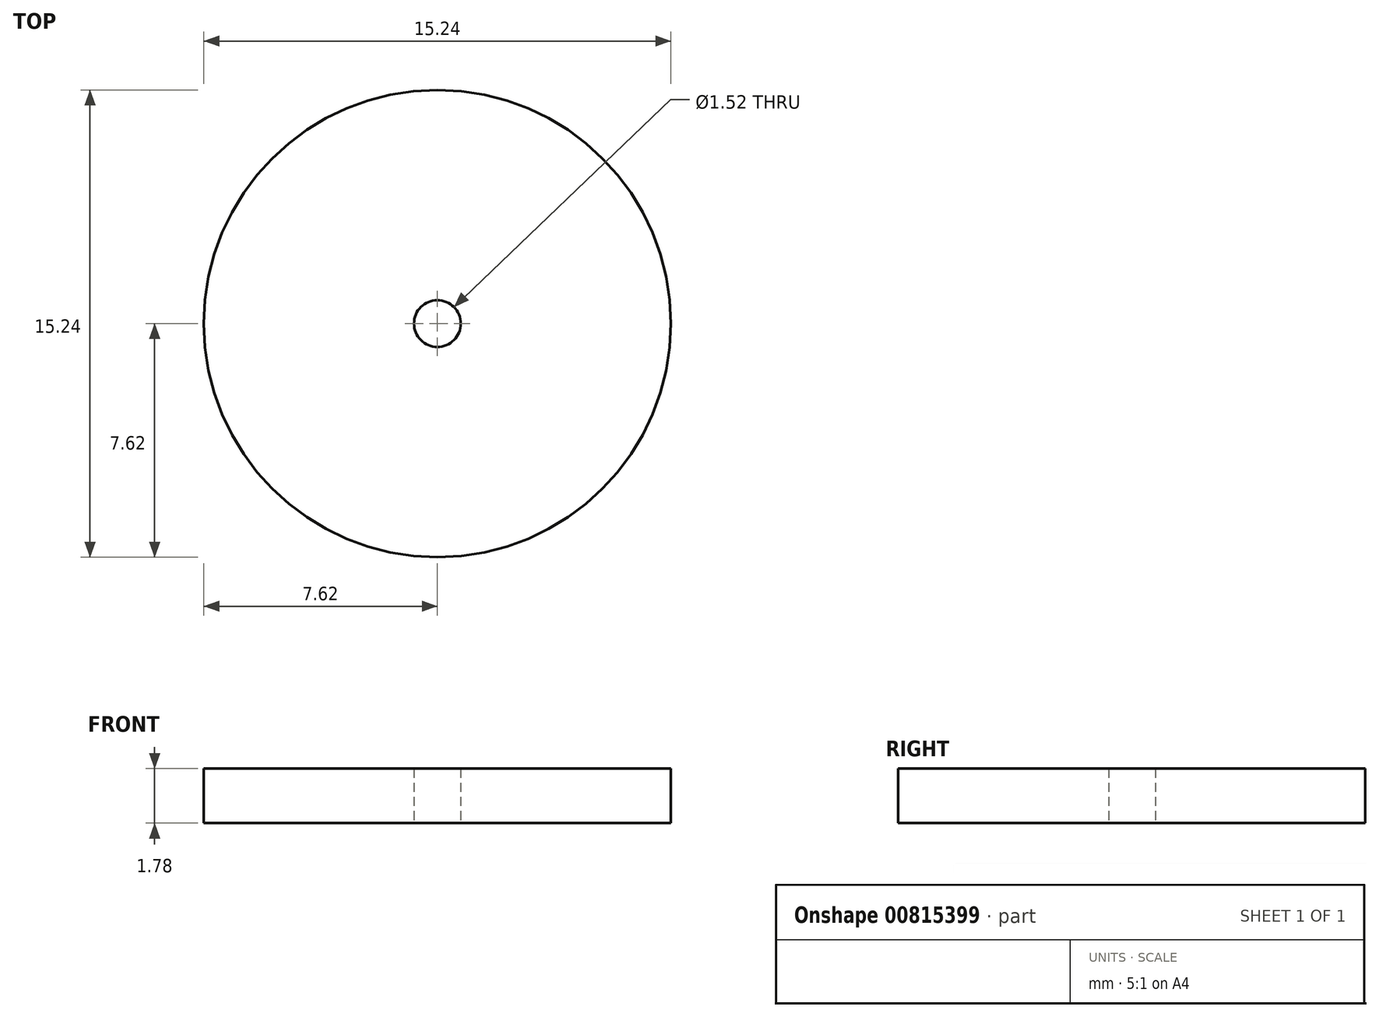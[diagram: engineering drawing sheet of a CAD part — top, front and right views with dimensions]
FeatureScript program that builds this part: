
annotation { "Feature Type Name" : "Feature", "Feature Type Description" : "" }
export const myFeature = defineFeature(function(context is Context, id is Id, definition is map)
    precondition{}
    {
        {
            var Q0;
            Q0=qCreatedBy(makeId("Top.planeOp"),FACE);
            var sketch = newSketch(context, id + "F0", { "sketchPlane" : qUnion([Q0])});
            skCircle(sketch, "E0", {"center": v(0, 0) * mm, "radius": 7.62 * mm});
            skCircle(sketch, "E1", {"center": v(0, 0) * mm, "radius": 0.76 * mm});
            skSolve(sketch);
        }
        {
            var Q0;
            Q0=qSketchRegion(id+"F0",true);
            extrude(context, id + "F1", {"entities" : qUnion([Q0]), "depth" : 1.78 * mm});
        }
    });
